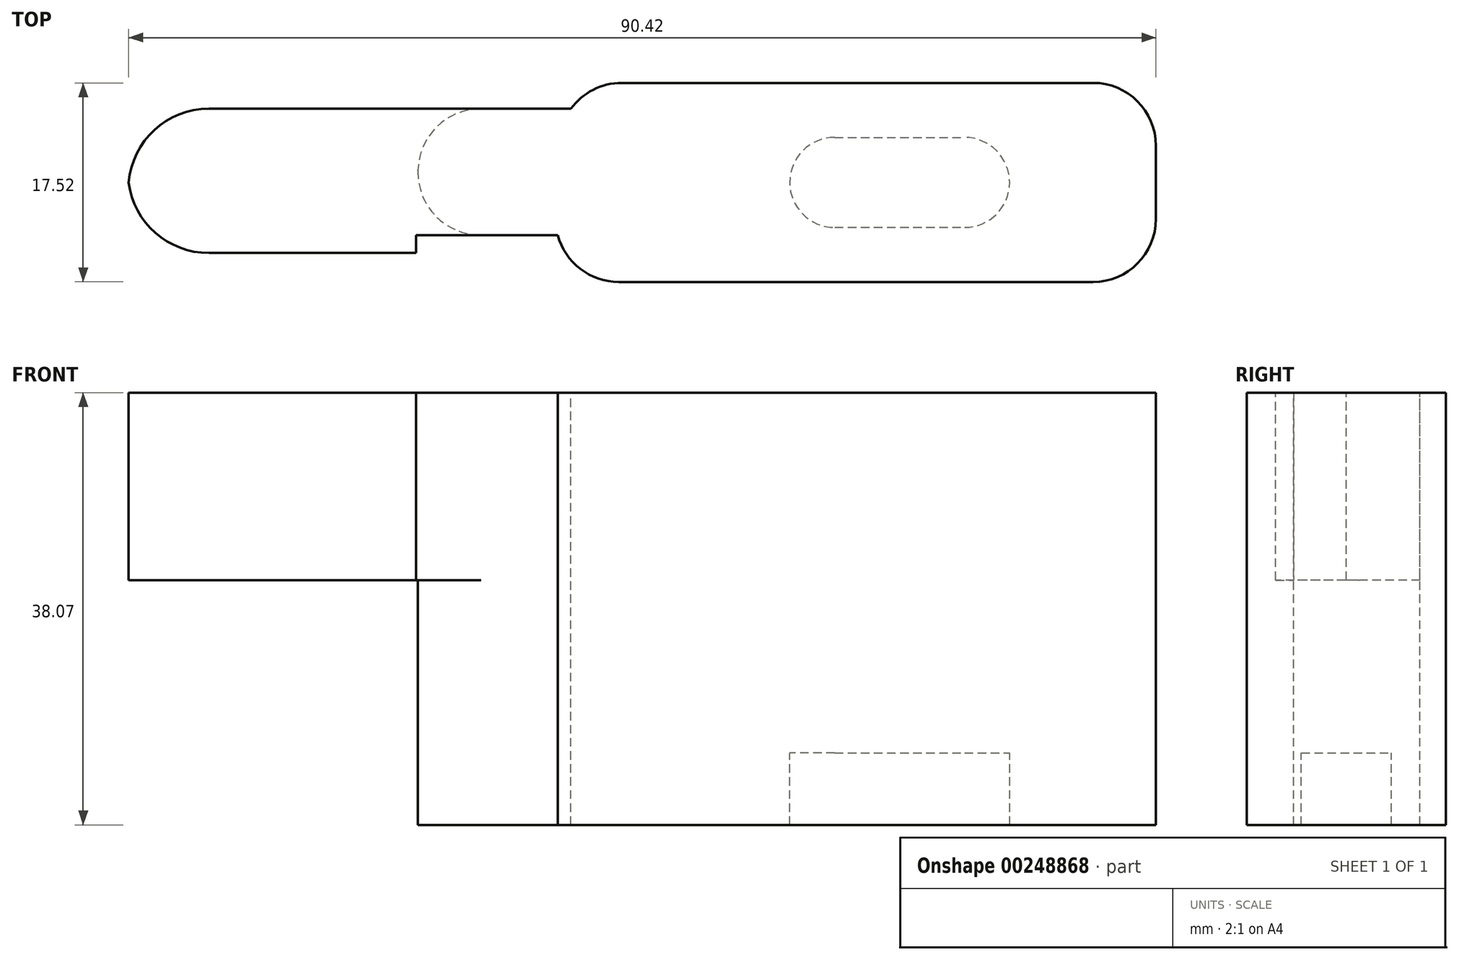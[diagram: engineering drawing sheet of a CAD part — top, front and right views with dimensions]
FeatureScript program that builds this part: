
annotation { "Feature Type Name" : "Feature", "Feature Type Description" : "" }
export const myFeature = defineFeature(function(context is Context, id is Id, definition is map)
    precondition{}
    {
        {
            var Q0;
            Q0=qCreatedBy(makeId("Top.planeOp"),FACE);
            var sketch = newSketch(context, id + "F0", { "sketchPlane" : qUnion([Q0])});
            skLineSegment(sketch, "E0.bottom", {"start": v(20.74, 8.76) * mm, "end": v(-20.74, 8.76) * mm});
            skLineSegment(sketch, "E0.top", {"start": v(20.74, -8.76) * mm, "end": v(-21.02, -8.76) * mm});
            skLineSegment(sketch, "E0.left", {"start": v(26.28, 3.23) * mm, "end": v(26.28, -3.23) * mm});
            skPoint(sketch, "E0.middle", {"position": v(0, 0) * mm});
            skPoint(sketch, "E1.visualSharp", {"position": v(26.28, 8.76) * mm});
            skArc(sketch, "E1.filletArc", {"start": v(26.28, 3.23) * mm, "mid": v(24.65, 7.14) * mm, "end": v(20.74, 8.76) * mm});
            skPoint(sketch, "E2.visualSharp", {"position": v(26.28, -8.76) * mm});
            skArc(sketch, "E2.filletArc", {"start": v(20.74, -8.76) * mm, "mid": v(24.65, -7.14) * mm, "end": v(26.28, -3.23) * mm});
            skPoint(sketch, "E3.visualSharp", {"position": v(-26.28, 8.76) * mm});
            skArc(sketch, "E3.filletArc", {"start": v(-20.74, 8.76) * mm, "mid": v(-23.25, 8.16) * mm, "end": v(-25.22, 6.48) * mm});
            skPoint(sketch, "E4.visualSharp", {"position": v(-26.28, -8.76) * mm});
            skArc(sketch, "E4.filletArc", {"start": v(-26.37, -4.64) * mm, "mid": v(-24.4, -7.61) * mm, "end": v(-21.02, -8.76) * mm});
            skLineSegment(sketch, "E5", {"start": v(-26.37, -4.64) * mm, "end": v(-38.84, -4.64) * mm});
            skLineSegment(sketch, "E6", {"start": v(-38.91, 6.48) * mm, "end": v(-25.22, 6.48) * mm});
            skLineSegment(sketch, "E7", {"start": v(-33.14, 6.48) * mm, "end": v(-38.91, 6.48) * mm});
            skLineSegment(sketch, "E8", {"start": v(-33.14, -4.64) * mm, "end": v(-38.84, -4.64) * mm});
            skLineSegment(sketch, "E9", {"start": v(-62.62, 0.95) * mm, "end": v(-62.62, 0.9) * mm});
            skPoint(sketch, "E10.visualSharp", {"position": v(-62.62, 6.48) * mm});
            skArc(sketch, "E10.filletArc", {"start": v(-57.09, 6.48) * mm, "mid": v(-61, 4.86) * mm, "end": v(-62.62, 0.95) * mm});
            skPoint(sketch, "E11.visualSharp", {"position": v(-62.62, -4.64) * mm});
            skArc(sketch, "E11.filletArc", {"start": v(-62.62, 0.9) * mm, "mid": v(-61, -3.02) * mm, "end": v(-57.09, -4.64) * mm});
            skLineSegment(sketch, "E12", {"start": v(-38.68, 1.05) * mm, "end": v(-38.68, 1.1) * mm});
            skPoint(sketch, "E12.startSnap0", {"position": v(-38.5, 7.57) * mm});
            skPoint(sketch, "E13.orphan", {"position": v(-38.5, 12.8) * mm});
            skPoint(sketch, "E14.orphan", {"position": v(-38.5, 2.34) * mm});
            skArc(sketch, "E15.filletArc", {"start": v(-38.68, 1.05) * mm, "mid": v(-37.12, -2.96) * mm, "end": v(-33.14, -4.64) * mm});
            skArc(sketch, "E16.filletArc", {"start": v(-33.14, 6.48) * mm, "mid": v(-37, 4.92) * mm, "end": v(-38.68, 1.1) * mm});
            skLineSegment(sketch, "E17", {"start": v(-57.09, 6.48) * mm, "end": v(-38.91, 6.48) * mm});
            skLineSegment(sketch, "E18", {"start": v(-38.84, -4.64) * mm, "end": v(-57.09, -4.64) * mm});
            skLineSegment(sketch, "E19", {"start": v(26.28, -3.23) * mm, "end": v(26.28, -27.27) * mm, "construction": true});
            skLineSegment(sketch, "E20", {"start": v(-62.62, 0.95) * mm, "end": v(-62.62, -24.18) * mm, "construction": true});
            skSolve(sketch);
        }
        {
            var Q0;
            Q0=makeQuery(id+"F0.imprint","IMPRINT",FACE,{"disambiguationData":[TD([[makeQuery(id+"F0.imprint","IMPRINT",EDGE,{"derivedFrom":sQuery(id+"F0.wireOp",EDGE,"E0.bottom")}),1.0]])]});
            extrude(context, id + "F1", {"entities" : qUnion([Q0]), "oppositeDirection" : true, "depth" : 31.72 * mm});
        }
        {
            var Q0;
            Q0=makeQuery(id+"F0.imprint","IMPRINT",FACE,{"disambiguationData":[TD([[makeQuery(id+"F0.imprint","IMPRINT",EDGE,{"derivedFrom":sQuery(id+"F0.wireOp",EDGE,"E9")}),1.0]])]});
            extrude(context, id + "F2", {"entities" : qUnion([Q0]), "operationType" : NewBodyOperationType.ADD, "oppositeDirection" : true, "depth" : 16.5 * mm});
        }
        {
            var Q0;
            Q0=makeQuery(id+"F1.opExtrude","CAP_FACE",FACE,{"disambiguationData":[OSD([sQuery(id+"F0.wireOp",EDGE,"E0.bottom"),sQuery(id+"F0.wireOp",EDGE,"E0.top"),sQuery(id+"F0.wireOp",EDGE,"E0.left"),sQuery(id+"F0.wireOp",EDGE,"E1.filletArc"),sQuery(id+"F0.wireOp",EDGE,"E2.filletArc"),sQuery(id+"F0.wireOp",EDGE,"E3.filletArc"),sQuery(id+"F0.wireOp",EDGE,"E4.filletArc"),sQuery(id+"F0.wireOp",EDGE,"E5"),sQuery(id+"F0.wireOp",EDGE,"E6"),sQuery(id+"F0.wireOp",EDGE,"E12"),sQuery(id+"F0.wireOp",EDGE,"E15.filletArc"),sQuery(id+"F0.wireOp",EDGE,"E16.filletArc"),sQuery(id+"F0.wireOp",EDGE,"E17"),sQuery(id+"F0.wireOp",EDGE,"E18")])],"isStart":false});
            var sketch = newSketch(context, id + "F3", { "sketchPlane" : qUnion([Q0])});
            skLineSegment(sketch, "E21", {"start": v(-2, 0) * mm, "end": v(9.44, 0) * mm});
            skArc(sketch, "E22.0.startCap", {"start": v(-2, -3.96) * mm, "mid": v(-5.96, 0) * mm, "end": v(-2, 3.96) * mm});
            skArc(sketch, "E22.0.endCap", {"start": v(9.44, 3.96) * mm, "mid": v(13.4, 0) * mm, "end": v(9.44, -3.96) * mm});
            skLineSegment(sketch, "E22.0.left", {"start": v(-2, 3.96) * mm, "end": v(9.44, 3.96) * mm});
            skLineSegment(sketch, "E22.0.right", {"start": v(-2, -3.96) * mm, "end": v(9.44, -3.96) * mm});
            skLineSegment(sketch, "E23", {"start": v(-5.96, 0) * mm, "end": v(-5.96, 17.95) * mm, "construction": true});
            skLineSegment(sketch, "E24", {"start": v(13.4, 0) * mm, "end": v(13.4, 18.25) * mm, "construction": true});
            skSolve(sketch);
        }
        {
            var Q0;
            Q0=makeQuery(id+"F3.imprint","IMPRINT",FACE,{"disambiguationData":[TD([[makeQuery(id+"F3.imprint","IMPRINT",EDGE,{"derivedFrom":sQuery(id+"F3.wireOp",EDGE,"E22.0.startCap")}),-1.0]])]});
            extrude(context, id + "F4", {"entities" : qUnion([Q0]), "operationType" : NewBodyOperationType.ADD, "depth" : 6.35 * mm});
        }
        {
            var Q0;
            Q0=qCreatedBy(makeId("Top.planeOp"),FACE);
            var sketch = newSketch(context, id + "F5", { "sketchPlane" : qUnion([Q0])});
            skArc(sketch, "E25.0", {"start": v(-64.14, 0) * mm, "mid": v(-61.79, -4.44) * mm, "end": v(-57.09, -6.22) * mm});
            skLineSegment(sketch, "E25.1", {"start": v(-38.84, -6.22) * mm, "end": v(-57.09, -6.22) * mm});
            skLineSegment(sketch, "E26", {"start": v(-38.84, -6.22) * mm, "end": v(-38.84, -4.6) * mm});
            skLineSegment(sketch, "E27", {"start": v(-38.84, -4.6) * mm, "end": v(-38.84, 6.48) * mm});
            skLineSegment(sketch, "E28", {"start": v(-38.84, 6.48) * mm, "end": v(-57.09, 6.48) * mm});
            skArc(sketch, "E29", {"start": v(-57.09, 6.48) * mm, "mid": v(-61.88, 4.62) * mm, "end": v(-64.14, 0) * mm});
            skSolve(sketch);
        }
        {
            var Q0;
            Q0=makeQuery(id+"F5.imprint","IMPRINT",FACE,{"disambiguationData":[TD([[makeQuery(id+"F5.imprint","IMPRINT",EDGE,{"derivedFrom":sQuery(id+"F5.wireOp",EDGE,"E25.0")}),1.0]])]});
            var Q1;
            Q1=sQuery(id+"F0.wireOp",EDGE,"E18");
            var Q2;
            Q2=sQuery(id+"F0.wireOp",EDGE,"E11.filletArc");
            var Q3;
            Q3=sQuery(id+"F0.wireOp",EDGE,"E10.filletArc");
            var Q4;
            Q4=sQuery(id+"F5.wireOp",EDGE,"E29");
            var Q5;
            Q5=sQuery(id+"F5.wireOp",EDGE,"E25.0");
            var Q6;
            Q6=sQuery(id+"F5.wireOp",EDGE,"E25.1");
            var Q7;
            Q7=sQuery(id+"F5.wireOp",EDGE,"E26");
            extrude(context, id + "F6", {"entities" : qUnion([Q0]), "operationType" : NewBodyOperationType.ADD, "surfaceEntities" : qUnion([Q1, Q2, Q3, Q4, Q5, Q6, Q7]), "oppositeDirection" : true, "depth" : 16.51 * mm});
        }
    });
